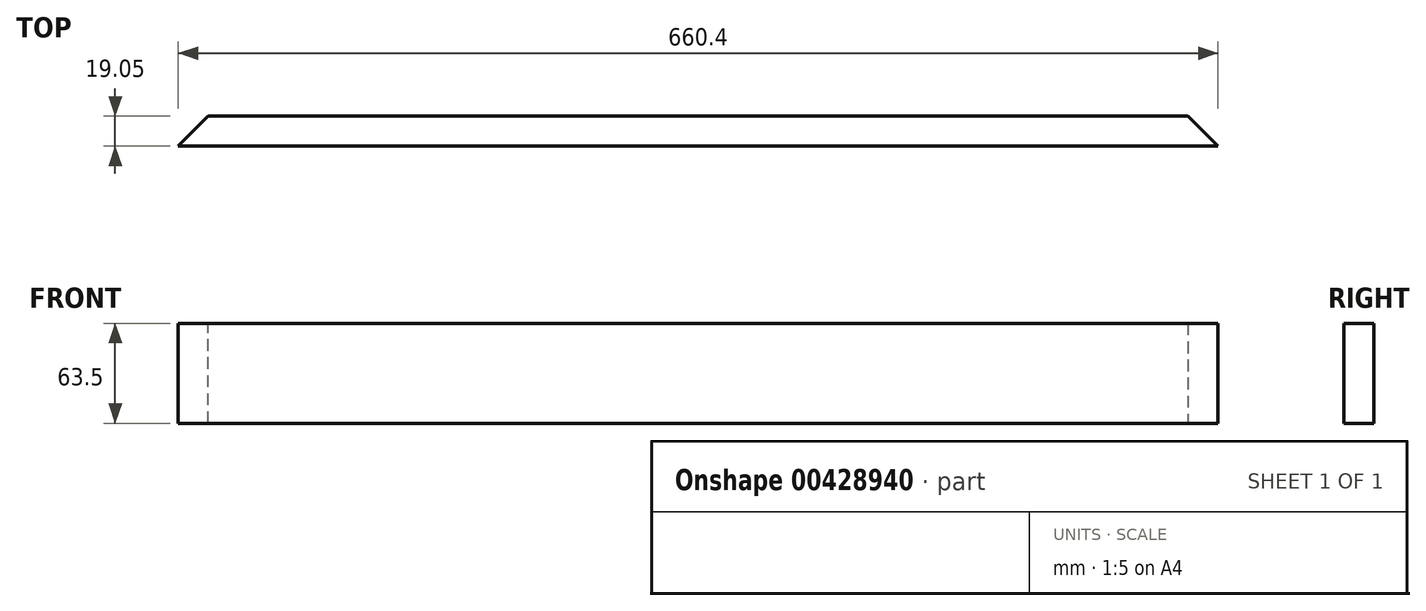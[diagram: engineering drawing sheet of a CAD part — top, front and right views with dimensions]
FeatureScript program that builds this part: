
annotation { "Feature Type Name" : "Feature", "Feature Type Description" : "" }
export const myFeature = defineFeature(function(context is Context, id is Id, definition is map)
    precondition{}
    {
        {
            var Q0;
            Q0=qCreatedBy(makeId("Front.planeOp"),FACE);
            var sketch = newSketch(context, id + "F0", { "sketchPlane" : qUnion([Q0])});
            skLineSegment(sketch, "E0.bottom", {"start": v(-114.8, 0) * mm, "end": v(545.6, 0) * mm});
            skLineSegment(sketch, "E0.top", {"start": v(-114.8, -63.5) * mm, "end": v(545.6, -63.5) * mm});
            skLineSegment(sketch, "E0.left", {"start": v(-114.8, 0) * mm, "end": v(-114.8, -63.5) * mm});
            skLineSegment(sketch, "E0.right", {"start": v(545.6, 0) * mm, "end": v(545.6, -63.5) * mm});
            skSolve(sketch);
        }
        {
            var Q0;
            Q0=makeQuery(id+"F0.imprint","IMPRINT",FACE,{"disambiguationData":[TD([[makeQuery(id+"F0.imprint","IMPRINT",EDGE,{"derivedFrom":sQuery(id+"F0.wireOp",EDGE,"E0.bottom")}),-1.0]])]});
            extrude(context, id + "F1", {"entities" : qUnion([Q0]), "depth" : 19.05 * mm});
        }
        {
            var Q0;
            Q0=makeQuery(id+"F1.opExtrude","CAP_EDGE",EDGE,{"disambiguationData":[OSD([sQuery(id+"F0.wireOp",EDGE,"E0.left")])],"isStart":true});
            var Q1;
            Q1=makeQuery(id+"F1.opExtrude","CAP_EDGE",EDGE,{"disambiguationData":[OSD([sQuery(id+"F0.wireOp",EDGE,"E0.right")])],"isStart":true});
            chamfer(context, id + "F2", {"entities" : qUnion([Q0, Q1]), "width" : 19.05 * mm, "tangentPropagation" : true});
        }
    });
